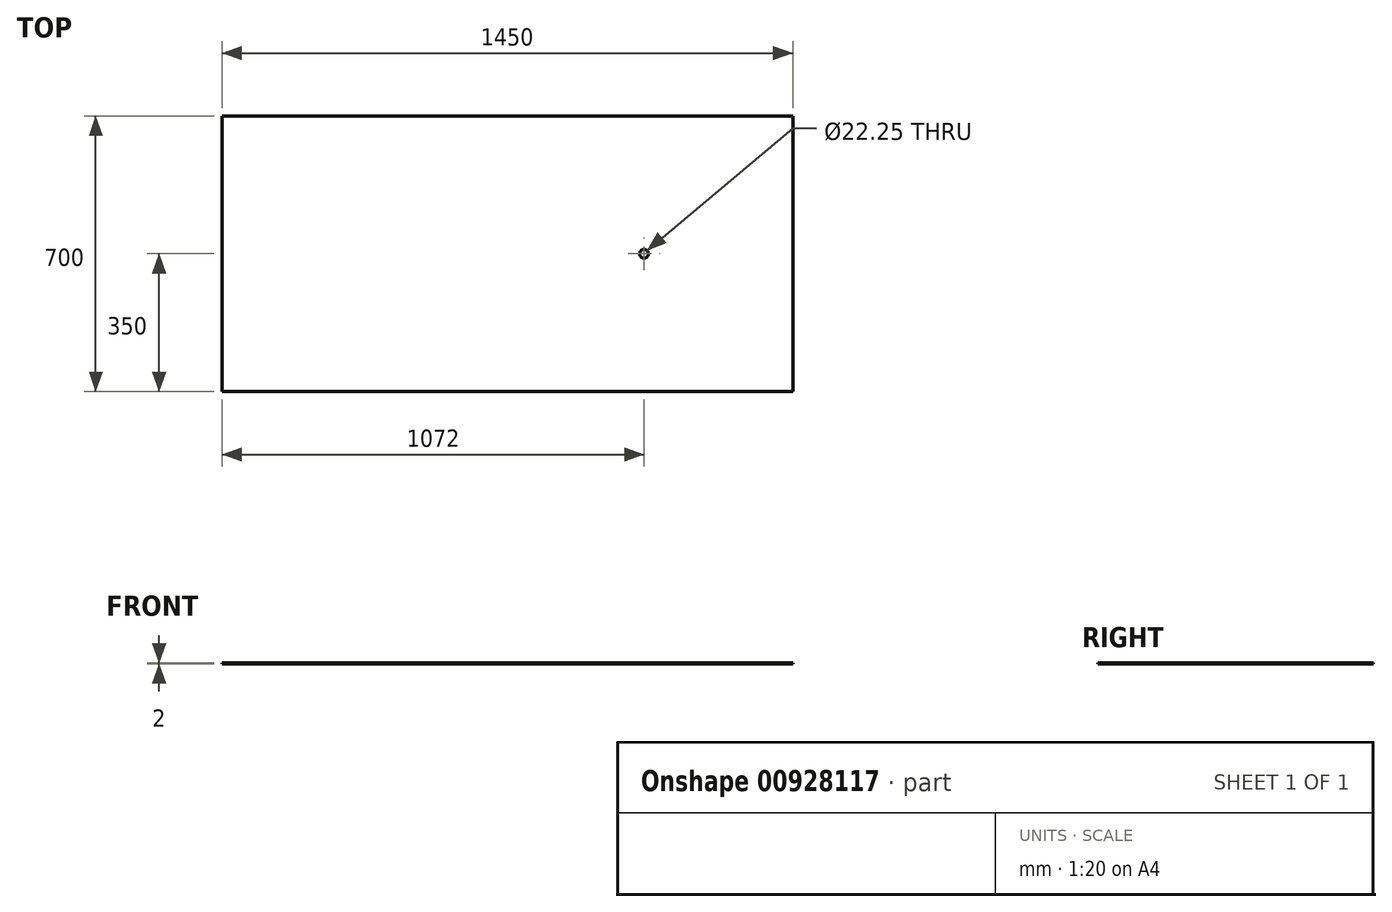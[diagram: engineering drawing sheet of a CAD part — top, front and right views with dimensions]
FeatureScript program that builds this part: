
annotation { "Feature Type Name" : "Feature", "Feature Type Description" : "" }
export const myFeature = defineFeature(function(context is Context, id is Id, definition is map)
    precondition{}
    {
        {
            var Q0;
            Q0=qCreatedBy(makeId("Top.planeOp"),FACE);
            var sketch = newSketch(context, id + "F0", { "sketchPlane" : qUnion([Q0])});
            skLineSegment(sketch, "E0.bottom", {"start": v(0, 0) * mm, "end": v(1450, 0) * mm});
            skLineSegment(sketch, "E0.top", {"start": v(0, 700) * mm, "end": v(1450, 700) * mm});
            skLineSegment(sketch, "E0.left", {"start": v(0, 0) * mm, "end": v(0, 700) * mm});
            skLineSegment(sketch, "E0.right", {"start": v(1450, 0) * mm, "end": v(1450, 700) * mm});
            skSolve(sketch);
        }
        {
            var Q0;
            Q0=makeQuery(id+"F0.imprint","IMPRINT",FACE,{"disambiguationData":[TD([[makeQuery(id+"F0.imprint","IMPRINT",EDGE,{"derivedFrom":sQuery(id+"F0.wireOp",EDGE,"E0.bottom")}),1.0]])]});
            extrude(context, id + "F1", {"entities" : qUnion([Q0]), "depth" : 2 * mm, "offsetDistance" : 25 * mm});
        }
        {
            var Q0;
            Q0=makeQuery(id+"F1.opExtrude","CAP_FACE",FACE,{"disambiguationData":[OSD([sQuery(id+"F0.wireOp",EDGE,"E0.bottom"),sQuery(id+"F0.wireOp",EDGE,"E0.top"),sQuery(id+"F0.wireOp",EDGE,"E0.left"),sQuery(id+"F0.wireOp",EDGE,"E0.right")])],"isStart":false});
            var sketch = newSketch(context, id + "F2", { "sketchPlane" : qUnion([Q0])});
            skLineSegment(sketch, "E1", {"start": v(0, 350) * mm, "end": v(1072, 350) * mm});
            skSolve(sketch);
        }
        {
            var Q0;
            Q0=sQuery(id+"F2.wireOp",VERTEX,"E1.end");
            var Q1;
            Q1=makeQuery(id+"F1.opExtrude","SWEPT_BODY",BODY,{"disambiguationData":[OSD([sQuery(id+"F0.wireOp",EDGE,"E0.bottom"),sQuery(id+"F0.wireOp",EDGE,"E0.top"),sQuery(id+"F0.wireOp",EDGE,"E0.left"),sQuery(id+"F0.wireOp",EDGE,"E0.right")])]});
            hole(context, id + "F3", {"style" : HoleStyle.C_BORE, "endStyle" : HoleEndStyle.BLIND, "standardTappedOrClearance" : lookupTablePath({ "fit" : "Normal", "standard" : "ISO", "size" : "M14", "type" : "Clearance" }), "standardBlindInLast" : lookupTablePath({ "fit" : "Normal", "standard" : "ISO", "size" : "M14", "type" : "Clearance" }), "holeDiameter" : 15.5 * mm, "cBoreDiameter" : 22.25 * mm, "cBoreDepth" : 14 * mm, "majorDiameter" : 5 * mm, "holeDepth" : 14 * mm, "isTappedThrough" : true, "tappedDepth" : 12 * mm, "tapClearance" : 3, "locations" : qUnion([Q0]), "scope" : qUnion([Q1])});
        }
    });
